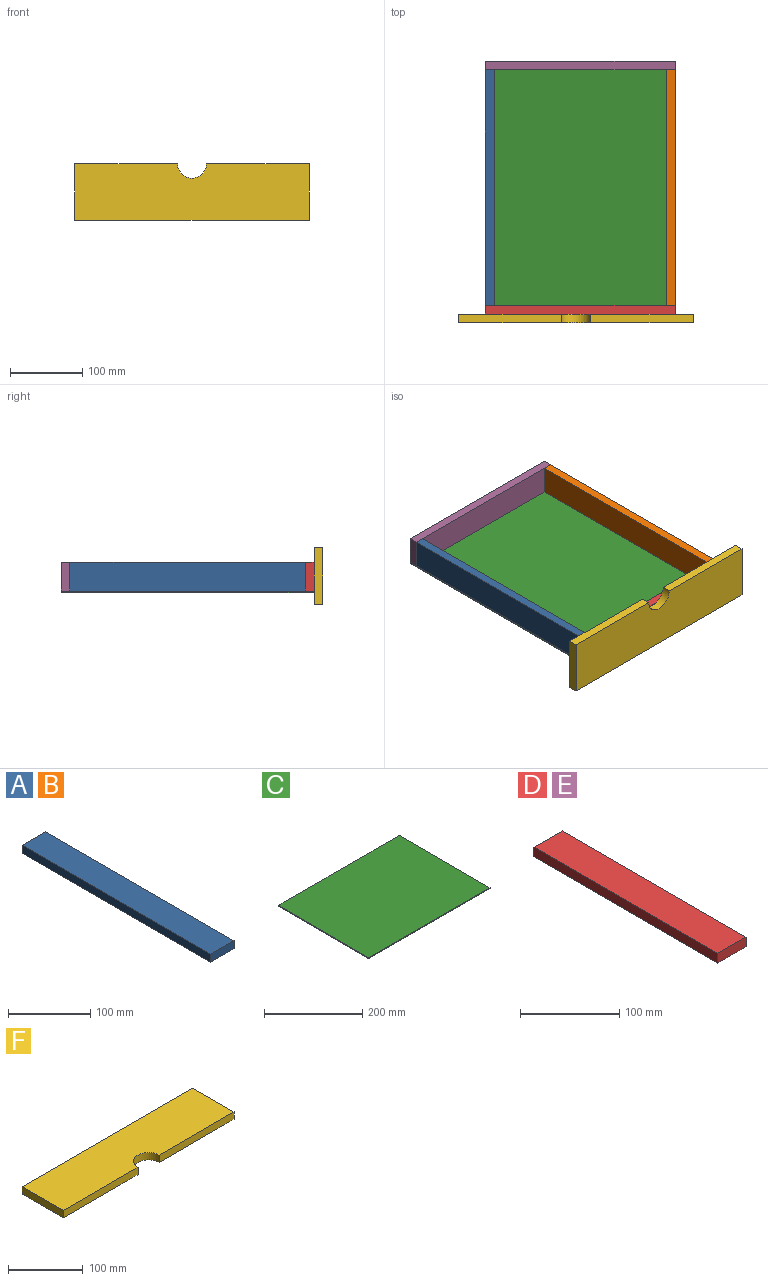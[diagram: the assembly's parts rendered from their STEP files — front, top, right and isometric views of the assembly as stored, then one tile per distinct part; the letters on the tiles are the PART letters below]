
ASSEMBLY  parts=6 mates=5
PART A: 6 faces, bbox 40x325x12 mm
  f0: plane 40x12mm, normal (0,1,0), area 480mm2, adj f1,f3,f4,f5
  f1: plane 325x12mm, normal (-1,0,0), area 3900mm2, adj f0,f2,f4,f5
  f2: plane 40x12mm, normal (0,-1,0), area 480mm2, adj f1,f3,f4,f5
  f3: plane 325x12mm, normal (1,0,0), area 3900mm2, adj f0,f2,f4,f5
  f4: plane 325x40mm, normal (0,0,1), area 13000mm2, adj f0,f1,f2,f3
  f5: plane 325x40mm, normal (0,0,-1), area 13000mm2, adj f0,f1,f2,f3
PART B: same geometry as A
PART C: 6 faces, bbox 349x262x2 mm
  f0: plane 349x2mm, normal (0,1,0), area 698mm2, adj f1,f3,f4,f5
  f1: plane 262x2mm, normal (-1,0,0), area 524mm2, adj f0,f2,f4,f5
  f2: plane 349x2mm, normal (0,-1,0), area 698mm2, adj f1,f3,f4,f5
  f3: plane 262x2mm, normal (1,0,0), area 524mm2, adj f0,f2,f4,f5
  f4: plane 349x262mm, normal (0,0,1), area 91438mm2, adj f0,f1,f2,f3
  f5: plane 349x262mm, normal (0,0,-1), area 91438mm2, adj f0,f1,f2,f3
PART D: 6 faces, bbox 40x262x12 mm
  f0: plane 40x12mm, normal (0,1,0), area 480mm2, adj f1,f3,f4,f5
  f1: plane 262x12mm, normal (-1,0,0), area 3144mm2, adj f0,f2,f4,f5
  f2: plane 40x12mm, normal (0,-1,0), area 480mm2, adj f1,f3,f4,f5
  f3: plane 262x12mm, normal (1,0,0), area 3144mm2, adj f0,f2,f4,f5
  f4: plane 262x40mm, normal (0,0,1), area 10480mm2, adj f0,f1,f2,f3
  f5: plane 262x40mm, normal (0,0,-1), area 10480mm2, adj f0,f1,f2,f3
PART E: same geometry as D
PART F: 8 faces, bbox 324x78x12 mm
  f0: plane 142x12mm, normal (0,-1,0), area 1704mm2, adj f2,f5,f6,f7
  f1: plane 324x12mm, normal (0,1,0), area 3888mm2, adj f2,f4,f5,f6
  f2: plane 78x12mm, normal (-1,0,0), area 936mm2, adj f0,f1,f5,f6
  f3: plane 142x12mm, normal (0,-1,0), area 1704mm2, adj f4,f5,f6,f7
  f4: plane 78x12mm, normal (1,0,0), area 936mm2, adj f1,f3,f5,f6
  f5: plane 324x78mm, normal (0,0,1), area 24643.7mm2, adj f0,f1,f2,f3,f4,f7
  f6: plane 324x78mm, normal (0,0,-1), area 24643.7mm2, adj f0,f1,f2,f3,f4,f7
  f7: cylinder r=20mm len=40mm, axis (0,0,1), area 754mm2, adj f0,f3,f5,f6
PLACE A rot(axis=(0,1,0),90deg) t=(-258.43,-79.93,-19.16)mm fixed
PLACE B rot(axis=(0.71,0,0.71),180deg) t=(-8.43,245.07,211.13)mm
PLACE C rot(axis=(-0.71,-0.71,0),180deg) t=(193.94,-611.38,75.98)mm
PLACE D rot(axis=(0.58,-0.58,0.58),120deg) t=(-12.9,-79.93,-3.85)mm
PLACE E rot(axis=(0.58,-0.58,0.58),120deg) t=(-12.9,257.07,-3.85)mm
PLACE F rot(axis=(-1,0,0),90deg) t=(381.8,-103.93,-65.09)mm
MATE fastened B.f0 <-> D.f5  axis (0,-1,0) through (3.57,-79.93,95.98)mm
MATE fastened D.f5 <-> A.f2  axis (0,1,0) through (-258.43,-79.93,95.98)mm
MATE fastened C.f5 <-> D.f1  axis (0,0,1) through (-258.43,-91.93,75.98)mm
MATE fastened F.f5 <-> D.f4  axis (0,1,0) through (-133.43,-91.93,95.98)mm
MATE fastened E.f4 <-> A.f0  axis (0,-1,0) through (-258.43,245.07,95.98)mm
